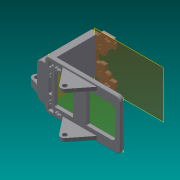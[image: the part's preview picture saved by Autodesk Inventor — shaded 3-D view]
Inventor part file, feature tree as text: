
AUTODESK INVENTOR PART (.ipt)
format: ipt  version: 2013 SP2 (Build 170200200, 200)  size: 969,216 bytes
history: native  units: in
note: dims shown in document units (in); Inventor stores cm internally (conversion verified against a paired STEP export)
features: extrude x23, fillet x21, sketch x19, reference x6, projected_geometry x4, plane x2
ambient origin geometry x8: Origin, YZ Plane, XZ Plane, XY Plane, X Axis, Y Axis, Z Axis, Center Point
bodies: Solid1 (feature_tree)
feature tree (75):
  plane  "Work Plane1"
  extrude  "Extrusion1"  Depth=0.125in
  fillet  "Fillet1"  Radius=0.4625in
  sketch  "Sketch2"  dims[d13=0.0in d14=0.925in]
  extrude  "Extrusion2"  Depth=0.925in
  extrude  "Extrusion3"  Depth=0.0938in TaperAngle=0.0deg
  extrude  "Extrusion4"  Depth=0.0938in TaperAngle=0.0deg
  extrude  "Extrusion5"  Depth=0.118in
  extrude  "Extrusion6"  Depth=0.118in
  extrude  "Extrusion7"  Depth=1.0in TaperAngle=0.0deg
  plane  "Work Plane2"
  extrude  "Extrusion9"  Depth=2.0in TaperAngle=0.0deg
  extrude  "Extrusion10"  Depth=2.3in TaperAngle=0.0deg
  extrude  "Extrusion11"  Depth=2.3in TaperAngle=0.0deg
  sketch  "Sketch8"  dims[d34=0.0938in d35=0.0in d36=1.0in d37=0.0in]
  extrude  "Extrusion12"  Depth=0.0938in TaperAngle=0.0deg
  extrude  "Extrusion13"  Depth=0.125in
  extrude  "Extrusion14"  Depth=0.125in
  extrude  "Extrusion15"  Depth=0.03in
  extrude  "Extrusion16"  Depth=0.03in
  extrude  "Extrusion17"  Depth=0.03in
  fillet  "Fillet2"  Radius=0.03in
  fillet  "Fillet3"  Radius=1.5in
  fillet  "Fillet4"  Radius=5.0in
  fillet  "Fillet5"  Radius=0.025in
  fillet  "Fillet6"  Radius=0.025in
  fillet  "Fillet7"  Radius=0.1in
  fillet  "Fillet8"  Radius=0.2in
  fillet  "Fillet9"  Radius=1.0in
  fillet  "Fillet10"  Radius=1.0in
  fillet  "Fillet11"  Radius=0.389in
  fillet  "Fillet12"  Radius=1.45in
  extrude  "Extrusion18"  Depth=0.01in
  extrude  "Extrusion19"  Depth=0.05in
  fillet  "Fillet13"  Radius=0.05in
  fillet  "Fillet14"  Radius=0.005in
  extrude  "Extrusion20"  [1 undecoded]
  extrude  "Extrusion21"  [1 undecoded]
  extrude  "Extrusion22"  [1 undecoded]
  extrude  "Extrusion23"  [1 undecoded]
  extrude  "Extrusion24"  [1 undecoded]
  fillet  "Fillet15"  [1 undecoded]
  fillet  "Fillet16"  [1 undecoded]
  fillet  "Fillet17"  [1 undecoded]
  fillet  "Fillet18"  [1 undecoded]
  fillet  "Fillet19"  [1 undecoded]
  fillet  "Fillet20"  [1 undecoded]
  fillet  "Fillet21"  [1 undecoded]
  sketch  "Sketch1"  dims[d4=0.0938in d5=0.0in d6=0.125in d12=0.4625in]
  reference  "Reference1"
  reference  "Reference2"
  reference  "Reference3"
  sketch  "Sketch3"  dims[d16=0.0938in d17=0.0in d18=0.0938in d19=0.0in]
  sketch  "Sketch4"  dims[d20=0.0938in d21=0.0in d22=0.0938in d23=0.0in]
  reference  "Reference4"
  reference  "Reference5"
  reference  "Reference6"
  sketch  "Sketch6"  dims[d24=0.52in d25=0.0in d27=0.118in]
  sketch  "Sketch7"  dims[d28=2.0in d29=0.0in d31=0.118in]
  projected_geometry  "Projected Loop1"
  sketch  "Sketch9"  dims[d38=1.0in d39=0.0in d40=2.0in d41=0.0in]
  sketch  "Sketch10"  dims[d42=2.0in d43=0.0in d44=2.3in d45=0.0in]
  sketch  "Sketch11"  dims[d46=0.2in d47=2.3in d48=0.0in]
  sketch  "Sketch12"  dims[d49=10.0in d50=0.0in d51=0.0938in d52=0.0in]
  projected_geometry  "Projected Loop2"
  sketch  "Sketch13"  dims[d53=0.125in d54=0.125in]
  projected_geometry  "Projected Loop3"
  sketch  "Sketch14"  dims[d55=0.125in d56=0.125in]
  sketch  "Sketch15"  dims[d57=0.03in d58=0.03in]
  sketch  "Sketch16"  dims[d59=0.03in d60=0.03in]
  sketch  "Sketch17"  dims[d61=0.03in d62=0.03in d63=0.03in d64=1.5in d65=0.0in d66=5.0in d67=0.0in d68=0.025in d69=0.025in d70=0.1in d71=0.0in d72=0.2in d74=1.0in d75=0.0in d78=1.0in d79=0.0in d80=0.389in d81=0.0in d82=1.45in d83=0.0in]
  sketch  "Sketch18"  dims[d84=0.025in d85=0.01in]
  sketch  "Sketch19"  dims[d86=0.025in d87=0.05in d88=0.05in d89=0.005in]
  sketch  "Sketch20"  dims[d90=0.005in]
  projected_geometry  "Projected Loop4"
note: 12 required parameter values undecoded (feature->parameter linkage not recoverable at this tier; creation-order binding heuristic only, values carry confidence <= 0.55)
